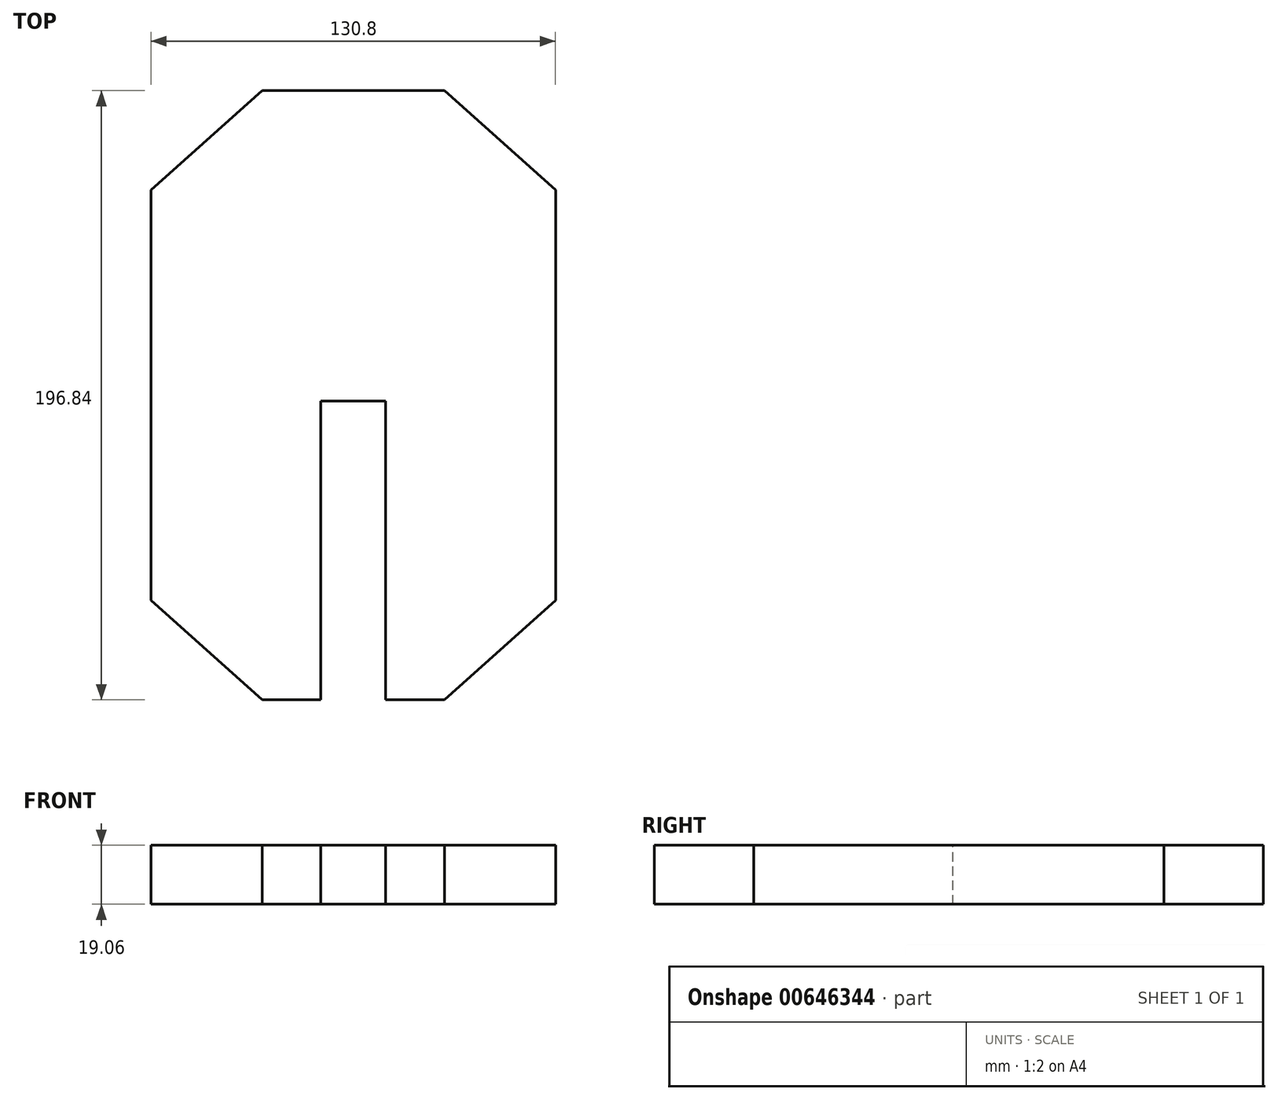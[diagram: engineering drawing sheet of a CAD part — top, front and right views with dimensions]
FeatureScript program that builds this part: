
annotation { "Feature Type Name" : "Feature", "Feature Type Description" : "" }
export const myFeature = defineFeature(function(context is Context, id is Id, definition is map)
    precondition{}
    {
        {
            var Q0;
            Q0=qCreatedBy(makeId("Top.planeOp"),FACE);
            var sketch = newSketch(context, id + "F0", { "sketchPlane" : qUnion([Q0])});
            skLineSegment(sketch, "E0.bottom", {"start": v(29.46, 98.42) * mm, "end": v(-29.46, 98.42) * mm});
            skLineSegment(sketch, "E0.top", {"start": v(29.46, -98.42) * mm, "end": v(-29.46, -98.42) * mm});
            skLineSegment(sketch, "E0.left", {"start": v(29.46, 98.42) * mm, "end": v(29.46, -98.42) * mm});
            skLineSegment(sketch, "E0.right", {"start": v(-29.46, 98.42) * mm, "end": v(-29.46, -98.42) * mm});
            skPoint(sketch, "E0.middle", {"position": v(0, 0) * mm});
            skLineSegment(sketch, "E1.bottom", {"start": v(-65.4, 66.3) * mm, "end": v(65.4, 66.3) * mm});
            skLineSegment(sketch, "E1.top", {"start": v(-65.4, -66.3) * mm, "end": v(65.4, -66.3) * mm});
            skLineSegment(sketch, "E1.left", {"start": v(-65.4, 66.3) * mm, "end": v(-65.4, -66.3) * mm});
            skLineSegment(sketch, "E1.right", {"start": v(65.4, 66.3) * mm, "end": v(65.4, -66.3) * mm});
            skLineSegment(sketch, "E2", {"start": v(-29.46, -98.42) * mm, "end": v(-65.4, -66.3) * mm});
            skLineSegment(sketch, "E3", {"start": v(29.46, -98.42) * mm, "end": v(65.4, -66.3) * mm});
            skLineSegment(sketch, "E4", {"start": v(65.4, 66.3) * mm, "end": v(29.46, 98.42) * mm});
            skLineSegment(sketch, "E5", {"start": v(-65.4, 66.3) * mm, "end": v(-29.46, 98.42) * mm});
            skSolve(sketch);
        }
        {
            var Q0;
            {var subQ0=sQuery(id+"F0.wireOp",EDGE,"E0.bottom");Q0=makeQuery(id+"F0.imprint","IMPRINT",FACE,{"disambiguationData":[TD([[makeQuery(id+"F0.imprint","IMPRINT",EDGE,{"derivedFrom":subQ0}),1.0]])]});}
            var Q1;
            {var subQ5=sQuery(id+"F0.wireOp",EDGE,"E1.left");Q1=makeQuery(id+"F0.imprint","IMPRINT",FACE,{"disambiguationData":[TD([[makeQuery(id+"F0.imprint","IMPRINT",EDGE,{"derivedFrom":subQ5}),1.0]])]});}
            var Q2;
            {var subQ0=sQuery(id+"F0.wireOp",EDGE,"E5");Q2=makeQuery(id+"F0.imprint","IMPRINT",FACE,{"disambiguationData":[TD([[makeQuery(id+"F0.imprint","IMPRINT",EDGE,{"derivedFrom":subQ0}),-1.0]])]});}
            var Q3;
            {var subQ0=sQuery(id+"F0.wireOp",EDGE,"E1.bottom");var subQ1=sQuery(id+"F0.wireOp",EDGE,"E0.left");var subQ2=makeQuery(id+"F0.imprint","INTERSECT",VERTEX,{"derivedFrom":[subQ1,subQ0]});Q3=makeQuery(id+"F0.imprint","IMPRINT",FACE,{"disambiguationData":[TD([[makeQuery(id+"F0.imprint","IMPRINT",EDGE,{"disambiguationData":[TD([[subQ2,-1.0]])],"derivedFrom":subQ1}),-1.0]])]});}
            var Q4;
            {var subQ5=sQuery(id+"F0.wireOp",EDGE,"E1.right");Q4=makeQuery(id+"F0.imprint","IMPRINT",FACE,{"disambiguationData":[TD([[makeQuery(id+"F0.imprint","IMPRINT",EDGE,{"derivedFrom":subQ5}),-1.0]])]});}
            var Q5;
            {var subQ0=sQuery(id+"F0.wireOp",EDGE,"E4");Q5=makeQuery(id+"F0.imprint","IMPRINT",FACE,{"disambiguationData":[TD([[makeQuery(id+"F0.imprint","IMPRINT",EDGE,{"derivedFrom":subQ0}),1.0]])]});}
            var Q6;
            {var subQ0=sQuery(id+"F0.wireOp",EDGE,"E3");Q6=makeQuery(id+"F0.imprint","IMPRINT",FACE,{"disambiguationData":[TD([[makeQuery(id+"F0.imprint","IMPRINT",EDGE,{"derivedFrom":subQ0}),1.0]])]});}
            var Q7;
            {var subQ0=sQuery(id+"F0.wireOp",EDGE,"E0.top");Q7=makeQuery(id+"F0.imprint","IMPRINT",FACE,{"disambiguationData":[TD([[makeQuery(id+"F0.imprint","IMPRINT",EDGE,{"derivedFrom":subQ0}),-1.0]])]});}
            var Q8;
            {var subQ0=sQuery(id+"F0.wireOp",EDGE,"E2");Q8=makeQuery(id+"F0.imprint","IMPRINT",FACE,{"disambiguationData":[TD([[makeQuery(id+"F0.imprint","IMPRINT",EDGE,{"derivedFrom":subQ0}),-1.0]])]});}
            extrude(context, id + "F1", {"entities" : qUnion([Q0, Q1, Q2, Q3, Q4, Q5, Q6, Q7, Q8]), "endBound" : BoundingType.SYMMETRIC, "depth" : 19.05 * mm, "offsetDistance" : 25.4 * mm});
        }
        {
            var Q0;
            Q0=qCreatedBy(makeId("Top.planeOp"),FACE);
            var sketch = newSketch(context, id + "F2", { "sketchPlane" : qUnion([Q0])});
            skLineSegment(sketch, "E6", {"start": v(-10.48, -98.42) * mm, "end": v(10.48, -98.42) * mm});
            skLineSegment(sketch, "E7", {"start": v(-10.48, -98.42) * mm, "end": v(-10.48, -1.9) * mm});
            skLineSegment(sketch, "E8", {"start": v(-10.48, -1.9) * mm, "end": v(10.48, -1.9) * mm});
            skLineSegment(sketch, "E9", {"start": v(10.48, -1.9) * mm, "end": v(10.48, -98.42) * mm});
            skSolve(sketch);
        }
        {
            var Q0;
            Q0=qSketchRegion(id+"F2",true);
            extrude(context, id + "F3", {"entities" : qUnion([Q0]), "operationType" : NewBodyOperationType.REMOVE, "endBound" : BoundingType.SYMMETRIC, "oppositeDirection" : true, "depth" : 19.05 * mm, "offsetDistance" : 25.4 * mm});
        }
    });
